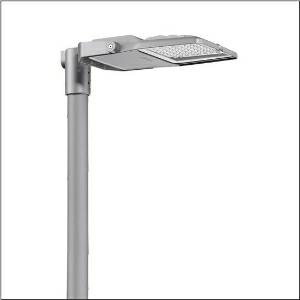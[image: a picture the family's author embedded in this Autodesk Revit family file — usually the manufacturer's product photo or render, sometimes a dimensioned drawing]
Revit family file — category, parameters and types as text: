
# Revit family: floodlight_fl_21_mini___pl64_5xa7771c2e3a_d2d4
name_source: partatom
category: Lighting Fixtures
units: mm (PartAtom-declared; Revit-internal decimal feet)

## family parameters
Cut with Voids When Loaded = No
Host = Face
Light Source = No
Part Type = Normal
Room Calculation Point = No
Round Connector Dimension = Use Diameter
Shared = No

## types (1)
- --- (1 x LED, 11790 lm, 87.2 W, 3000K)
    Apparent Load = 87 VA
    CIE Flux Codes = 28 80 98 100 100
    Color Rendering = 70
    Color Temperature = 3000K
    Default Elevation = 1800 mm
    Description = Floodlight FL 21 mini, floodlight, primary light control with lens, of PMMA, primary optical cover: protective disc, of toughened safety glass, transparent, light distribution: PL64, light emission: direct distribution, installation type: surface-mounted, LED, High Power LED, rated luminous flux: 11.790lm, luminous efficacy: 135lm/W, light colour: 730, colour temperature: 3000K, control gear: ECG iQ, control: Auto-Match, Temp-Guard, Lumen-Switch, Night-Set, Smart-Wire, Light-Fading, Desk-Remote (wireless, voltage-free reading and setting of iQ features in the workshop via application-optimized NFC function/RFID function), optimised constant luminous flux control (CLO 2.0), with terminal, 6-pole, mains connection: 220..240V, AC, 50/60Hz, start of lifetime: 87W, end of lifetime: 92W, reduction: 40W, luminaire housing, of diecast aluminium, powder-coated, Siteco® metallic grey (DB 702S), corrosivity category C5 according to DIN EN ISO 12944, mast bracket, of steel, galvanised, powder-coated, Siteco® metallic grey (DB 702S), protection rating (complete): IP66, insulation class (complete): insulation class II (safety insulation), certification: CE, ENEC, VDE, protection symbol: D, impact resistance: IK08, permissible operating ambient temperature: -40..+40°C, permissible operating ambient temperature for outdoor applications: -40..+50°C, standard: DIN EN 12944, packaging unit: 1 piece

Light Distribution: PL64
    Height = 70 mm
    Lamp = 1 x LED
    Lamp Light Flux = 11790 lm
    Lamp Power = 87.2 W
    Lamp count = 1
    Length = 485 mm
    Luminous efficacy = 135 lm/W
    Manufacturer = Siteco
    ModVariant = No
    Model = 5XA7771C2E3A
    Number of Poles = 1
    OnlyDefault = Yes
    Power Factor = 1
    Product Name = Floodlight FL 21 mini | PL64
    Product group = floodlight | pylon top
    ProductGroupID = 6101
    Protection Class = Protection class II
    Protection Degree = IP 66
    RLX_Detail_Level = 1
    RlxData = <blob elided: 101201 chars, md5=dd2fcb63>
    Socket = socket
    Standby Power = 0 W
    System Light Flux = 11790 lm
    System Power = 87 W
    Type Comments = factory setting: luminous flux: 100 % | dim-lin: 254 | 456 mA
    Type Image = l_1007125.jpg
    URL = http://relux.com
    VarID = @adj_077665
    Voltage = 0 V
    Weight = 0.00 kg
    Width = 337 mm

## geometry (parser evidence)
native form markers: Blend x4, Sweep x12
no freeform markers — native parametric forms only
